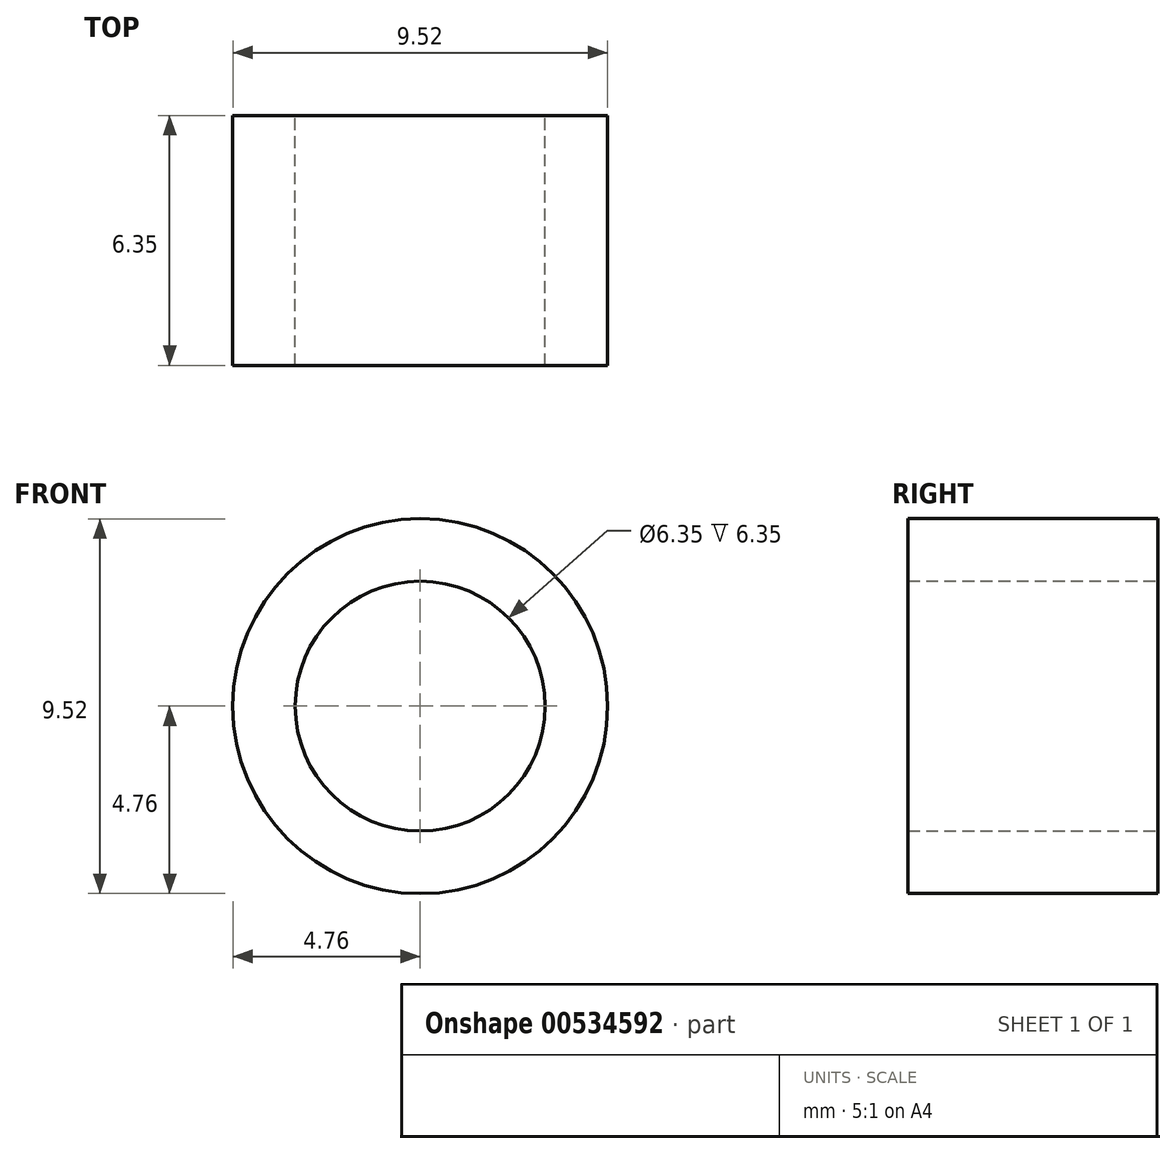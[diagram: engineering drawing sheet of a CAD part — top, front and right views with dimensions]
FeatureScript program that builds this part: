
annotation { "Feature Type Name" : "Feature", "Feature Type Description" : "" }
export const myFeature = defineFeature(function(context is Context, id is Id, definition is map)
    precondition{}
    {
        {
            var Q0;
            Q0=qCreatedBy(makeId("Front.planeOp"),FACE);
            var sketch = newSketch(context, id + "F0", { "sketchPlane" : qUnion([Q0])});
            skCircle(sketch, "E0", {"center": v(0, 0) * mm, "radius": 3.18 * mm});
            skCircle(sketch, "E1", {"center": v(0, 0) * mm, "radius": 4.76 * mm});
            skSolve(sketch);
        }
        {
            var Q0;
            Q0=makeQuery(id+"F0.imprint","IMPRINT",FACE,{"disambiguationData":[TD([[makeQuery(id+"F0.imprint","IMPRINT",EDGE,{"derivedFrom":sQuery(id+"F0.wireOp",EDGE,"E0")}),-1.0]])]});
            extrude(context, id + "F1", {"entities" : qUnion([Q0]), "depth" : 6.35 * mm, "offsetDistance" : 25.4 * mm});
        }
    });
